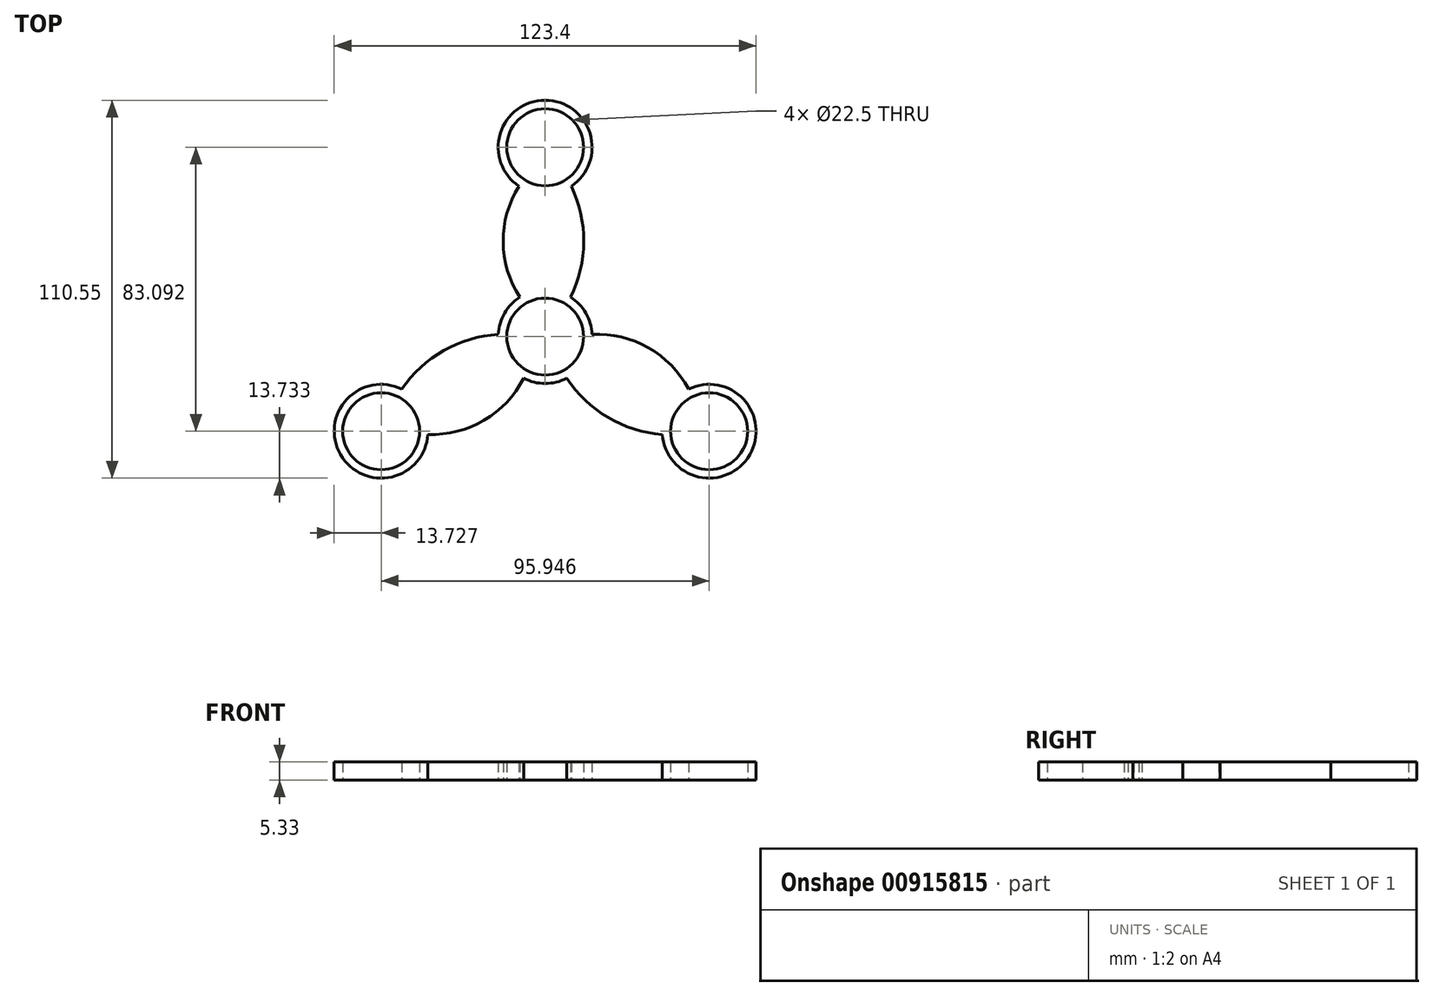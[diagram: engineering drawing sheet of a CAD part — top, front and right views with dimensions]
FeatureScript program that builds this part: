
annotation { "Feature Type Name" : "Feature", "Feature Type Description" : "" }
export const myFeature = defineFeature(function(context is Context, id is Id, definition is map)
    precondition{}
    {
        {
            var Q0;
            Q0=qCreatedBy(makeId("Top.planeOp"),FACE);
            var sketch = newSketch(context, id + "F0", { "sketchPlane" : qUnion([Q0])});
            skCircle(sketch, "E0", {"center": v(0, 0) * mm, "radius": 11.25 * mm});
            skCircle(sketch, "E1", {"center": v(0, 55.4) * mm, "radius": 11.25 * mm});
            skArc(sketch, "E2", {"start": v(7.66, 44) * mm, "mid": v(0, 69.12) * mm, "end": v(-7.66, 44) * mm});
            skArc(sketch, "E3", {"start": v(-7.4, 11.56) * mm, "mid": v(0, -13.73) * mm, "end": v(7.4, 11.56) * mm});
            skArc(sketch, "E4", {"start": v(-7.66, 44) * mm, "mid": v(-12.28, 27.74) * mm, "end": v(-7.4, 11.56) * mm});
            skArc(sketch, "E5", {"start": v(7.4, 11.56) * mm, "mid": v(11.3, 27.75) * mm, "end": v(7.66, 44) * mm});
            skArc(sketch, "E6.1.0", {"start": v(-41.94, -15.37) * mm, "mid": v(-59.86, -34.56) * mm, "end": v(-34.28, -28.64) * mm});
            skCircle(sketch, "E6.1.1", {"center": v(-47.97, -27.7) * mm, "radius": 11.25 * mm});
            skArc(sketch, "E6.1.2", {"start": v(-34.28, -28.64) * mm, "mid": v(-17.88, -24.5) * mm, "end": v(-6.3, -12.2) * mm});
            skArc(sketch, "E6.1.3", {"start": v(-13.71, 0.64) * mm, "mid": v(-29.68, -4.1) * mm, "end": v(-41.94, -15.37) * mm});
            skArc(sketch, "E6.2.0", {"start": v(34.28, -28.64) * mm, "mid": v(59.86, -34.56) * mm, "end": v(41.94, -15.37) * mm});
            skCircle(sketch, "E6.2.1", {"center": v(47.97, -27.7) * mm, "radius": 11.25 * mm});
            skArc(sketch, "E6.2.2", {"start": v(41.94, -15.37) * mm, "mid": v(30.17, -3.23) * mm, "end": v(13.71, 0.64) * mm});
            skArc(sketch, "E6.2.3", {"start": v(6.3, -12.2) * mm, "mid": v(18.39, -23.66) * mm, "end": v(34.28, -28.64) * mm});
            skSolve(sketch);
        }
        {
            var Q0;
            Q0=makeQuery(id+"F0.imprint","IMPRINT",FACE,{"disambiguationData":[TD([[makeQuery(id+"F0.imprint","IMPRINT",EDGE,{"derivedFrom":sQuery(id+"F0.wireOp",EDGE,"E0")}),-1.0]])]});
            var Q1;
            Q1=makeQuery(id+"F0.imprint","IMPRINT",FACE,{"disambiguationData":[TD([[makeQuery(id+"F0.imprint","IMPRINT",EDGE,{"derivedFrom":sQuery(id+"F0.wireOp",EDGE,"E6.1.0")}),1.0]])]});
            var Q2;
            Q2=makeQuery(id+"F0.imprint","IMPRINT",FACE,{"disambiguationData":[TD([[makeQuery(id+"F0.imprint","IMPRINT",EDGE,{"derivedFrom":sQuery(id+"F0.wireOp",EDGE,"E6.2.0")}),1.0]])]});
            extrude(context, id + "F1", {"entities" : qUnion([Q0, Q1, Q2]), "depth" : 5.33 * mm, "offsetDistance" : 25.4 * mm});
        }
    });
